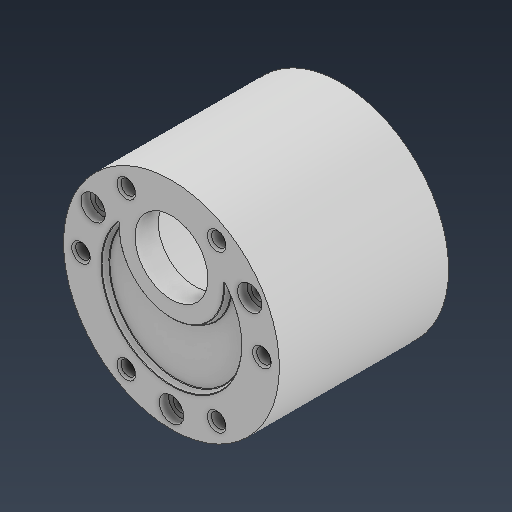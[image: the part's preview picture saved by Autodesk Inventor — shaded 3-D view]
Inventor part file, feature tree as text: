
AUTODESK INVENTOR PART (.ipt)
format: ipt  version: 2021 (Build 250183000, 183)  size: 204,288 bytes
history: native  units: in
note: dims shown in document units (in); Inventor stores cm internally (conversion verified against a paired STEP export)
features: fillet x1
ambient origin geometry x8: Origin, YZ Plane, XZ Plane, XY Plane, X Axis, Y Axis, Z Axis, Center Point
bodies: Solid1 (feature_tree)
feature tree (1):
  fillet  "Fillet1"  [1 undecoded]
note: 1 required parameter value undecoded (feature->parameter linkage not recoverable at this tier; creation-order binding heuristic only, values carry confidence <= 0.55)
